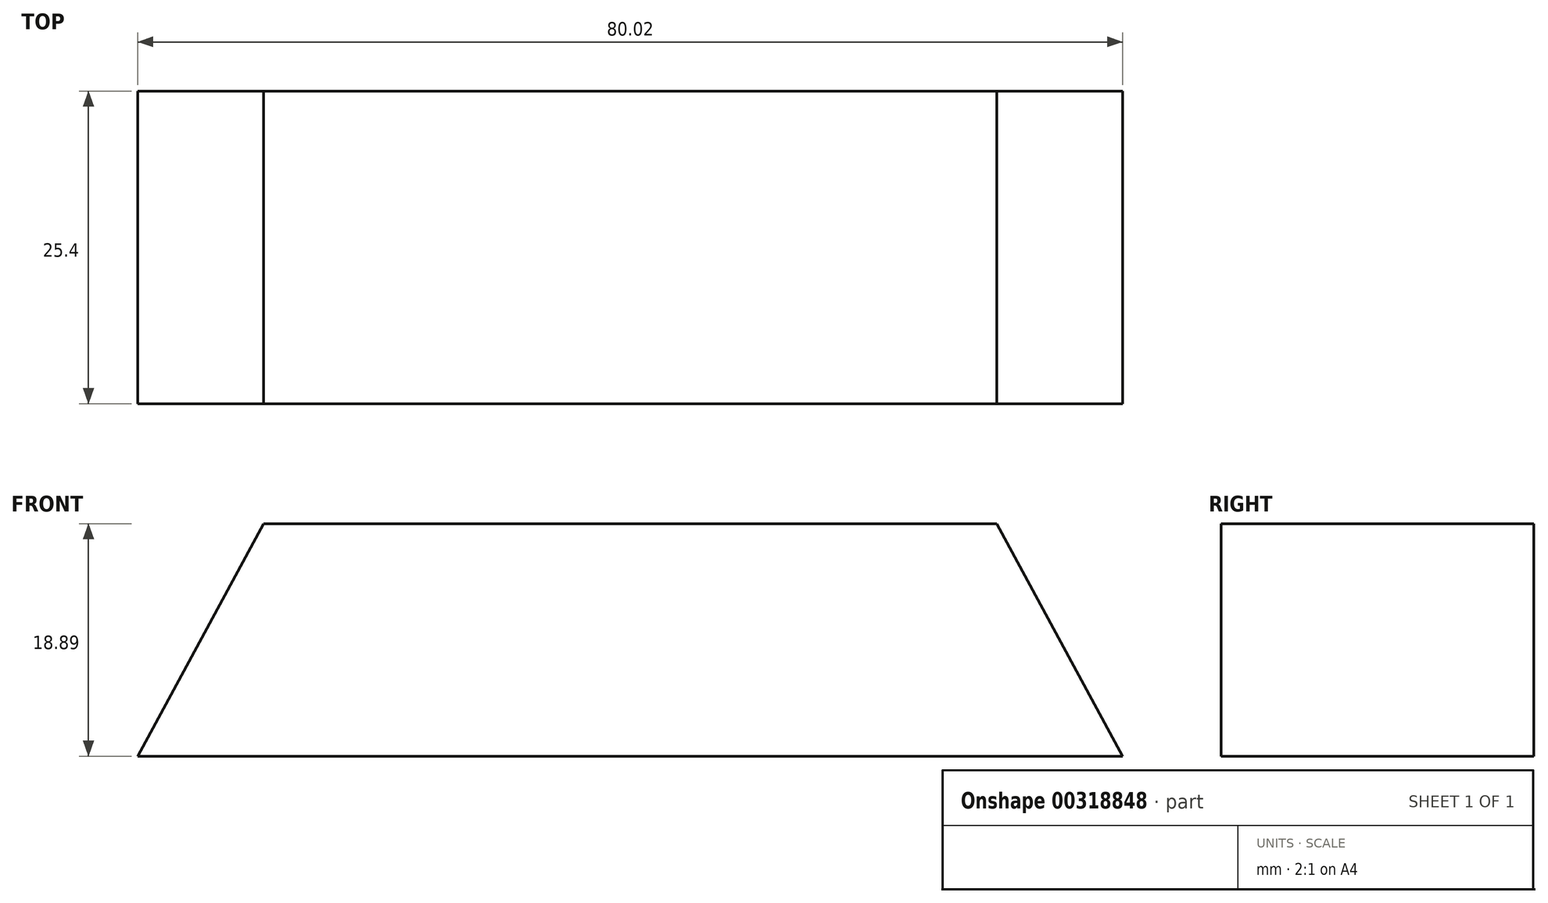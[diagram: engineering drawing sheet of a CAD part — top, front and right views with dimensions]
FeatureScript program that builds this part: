
annotation { "Feature Type Name" : "Feature", "Feature Type Description" : "" }
export const myFeature = defineFeature(function(context is Context, id is Id, definition is map)
    precondition{}
    {
        {
            var Q0;
            Q0=qCreatedBy(makeId("Front.planeOp"),FACE);
            var sketch = newSketch(context, id + "F0", { "sketchPlane" : qUnion([Q0])});
            skLineSegment(sketch, "E0", {"start": v(0, 0) * mm, "end": v(40, 0) * mm});
            skLineSegment(sketch, "E1", {"start": v(40, 0) * mm, "end": v(29.78, 18.9) * mm});
            skLineSegment(sketch, "E2", {"start": v(29.78, 18.9) * mm, "end": v(0, 18.9) * mm});
            skLineSegment(sketch, "E3.MirrorCS", {"start": v(-40, 0) * mm, "end": v(-29.78, 18.9) * mm});
            skLineSegment(sketch, "E4.MirrorCS", {"start": v(-29.78, 18.9) * mm, "end": v(0, 18.9) * mm});
            skLineSegment(sketch, "E5.MirrorCS", {"start": v(0, 0) * mm, "end": v(-40, 0) * mm});
            skSolve(sketch);
        }
        {
            var Q0;
            Q0=makeQuery(id+"F0.imprint","IMPRINT",FACE,{"disambiguationData":[TD([[makeQuery(id+"F0.imprint","IMPRINT",EDGE,{"derivedFrom":sQuery(id+"F0.wireOp",EDGE,"E0")}),1.0]])]});
            extrude(context, id + "F1", {"entities" : qUnion([Q0]), "endBound" : BoundingType.SYMMETRIC, "depth" : 25.4 * mm});
        }
        {
            var Q0;
            Q0=qCreatedBy(makeId("Top.planeOp"),FACE);
            var sketch = newSketch(context, id + "F2", { "sketchPlane" : qUnion([Q0])});
            skCircle(sketch, "E6", {"center": v(0, 0) * mm, "radius": 5 * mm});
            skSolve(sketch);
        }
        {
            var Q0;
            Q0=sQuery(id+"F2.wireOp",EDGE,"E6");
            extrude(context, id + "F3", {"bodyType" : ToolBodyType.SURFACE, "surfaceEntities" : qUnion([Q0]), "depth" : 76.2 * mm});
        }
    });
